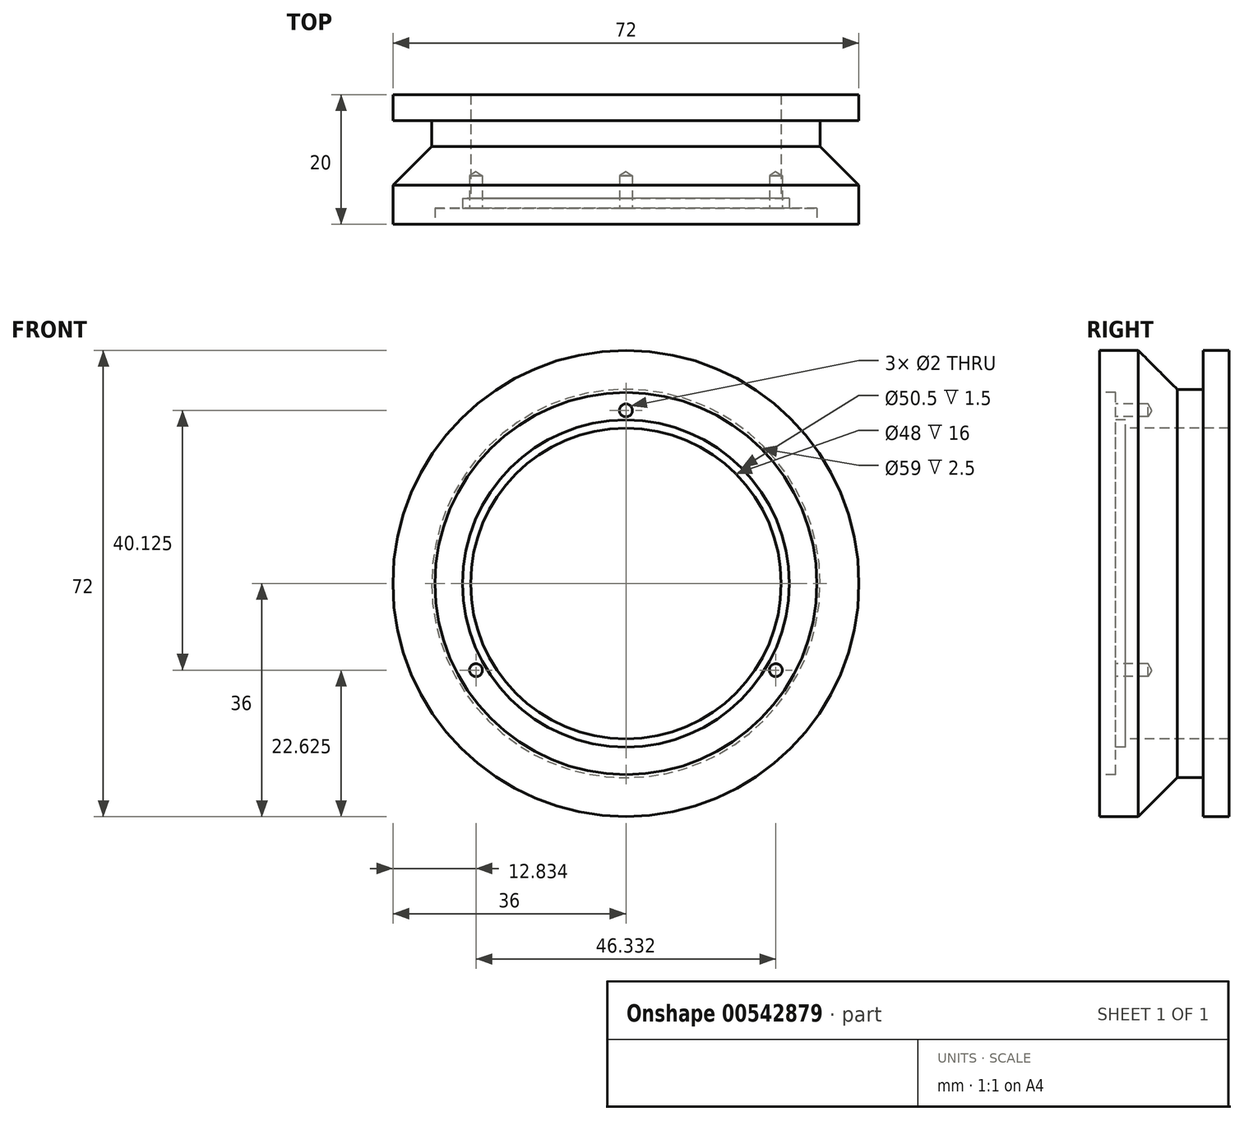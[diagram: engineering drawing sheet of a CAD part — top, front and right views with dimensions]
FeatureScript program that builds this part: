
annotation { "Feature Type Name" : "Feature", "Feature Type Description" : "" }
export const myFeature = defineFeature(function(context is Context, id is Id, definition is map)
    precondition{}
    {
        {
            var Q0;
            Q0=qCreatedBy(makeId("Right.planeOp"),FACE);
            var sketch = newSketch(context, id + "F0", { "sketchPlane" : qUnion([Q0])});
            skLineSegment(sketch, "E0", {"start": v(0, 0) * mm, "end": v(0, 36) * mm});
            skLineSegment(sketch, "E1", {"start": v(0, 36) * mm, "end": v(6, 36) * mm});
            skLineSegment(sketch, "E2", {"start": v(6, 36) * mm, "end": v(12, 30) * mm});
            skLineSegment(sketch, "E3", {"start": v(16, 36) * mm, "end": v(20, 36) * mm});
            skLineSegment(sketch, "E4", {"start": v(20, 36) * mm, "end": v(20, 0) * mm});
            skLineSegment(sketch, "E5", {"start": v(20, 0) * mm, "end": v(0, 0) * mm});
            skLineSegment(sketch, "E6", {"start": v(12, 30) * mm, "end": v(16, 30) * mm});
            skLineSegment(sketch, "E7", {"start": v(16, 30) * mm, "end": v(16, 36) * mm});
            skSolve(sketch);
        }
        {
            var Q0;
            Q0=makeQuery(id+"F0.imprint","IMPRINT",FACE,{"disambiguationData":[TD([[makeQuery(id+"F0.imprint","IMPRINT",EDGE,{"derivedFrom":sQuery(id+"F0.wireOp",EDGE,"E0")}),-1.0]])]});
            var Q1;
            Q1=sQuery(id+"F0.wireOp",EDGE,"E5");
            revolve(context, id + "F1", {"entities" : qUnion([Q0]), "axis" : qUnion([Q1]), "revolveType" : RevolveType.FULL});
        }
        {
            var Q0;
            Q0=makeQuery(id+"F1.opRevolve","SWEPT_FACE",FACE,{"disambiguationData":[OSD([sQuery(id+"F0.wireOp",EDGE,"E0")])]});
            var sketch = newSketch(context, id + "F2", { "sketchPlane" : qUnion([Q0])});
            skCircle(sketch, "E8", {"center": v(0, 0) * mm, "radius": 25.25 * mm});
            skSolve(sketch);
        }
        {
            var Q0;
            Q0=makeQuery(id+"F2.imprint","IMPRINT",FACE,{"disambiguationData":[TD([[makeQuery(id+"F2.imprint","IMPRINT",EDGE,{"derivedFrom":sQuery(id+"F2.wireOp",EDGE,"E8")}),1.0]])]});
            extrude(context, id + "F3", {"entities" : qUnion([Q0]), "operationType" : NewBodyOperationType.REMOVE, "oppositeDirection" : true, "depth" : 4 * mm, "offsetDistance" : 25 * mm});
        }
        {
            var Q0;
            Q0=makeQuery(id+"F3.boolean.opBoolean","COPY",FACE,{"derivedFrom":makeQuery(id+"F3.opExtrude","CAP_FACE",FACE,{"disambiguationData":[OSD([sQuery(id+"F2.wireOp",EDGE,"E8")])],"isStart":false})});
            var sketch = newSketch(context, id + "F4", { "sketchPlane" : qUnion([Q0])});
            skCircle(sketch, "E9", {"center": v(0, 0) * mm, "radius": 24 * mm});
            skSolve(sketch);
        }
        {
            var Q0;
            Q0=makeQuery(id+"F4.imprint","IMPRINT",FACE,{"disambiguationData":[TD([[makeQuery(id+"F4.imprint","IMPRINT",EDGE,{"derivedFrom":sQuery(id+"F4.wireOp",EDGE,"E9")}),1.0]])]});
            extrude(context, id + "F5", {"entities" : qUnion([Q0]), "operationType" : NewBodyOperationType.REMOVE, "endBound" : BoundingType.UP_TO_NEXT, "oppositeDirection" : true, "depth" : 25 * mm, "offsetDistance" : 25 * mm});
        }
        {
            var Q0;
            Q0=makeQuery(id+"F1.opRevolve","SWEPT_FACE",FACE,{"disambiguationData":[OSD([sQuery(id+"F0.wireOp",EDGE,"E0")])]});
            var sketch = newSketch(context, id + "F6", { "sketchPlane" : qUnion([Q0])});
            skCircle(sketch, "E10", {"center": v(0, 0) * mm, "radius": 29.5 * mm});
            skSolve(sketch);
        }
        {
            var Q0;
            Q0=makeQuery(id+"F6.imprint","IMPRINT",FACE,{"disambiguationData":[TD([[makeQuery(id+"F6.imprint","IMPRINT",EDGE,{"derivedFrom":sQuery(id+"F6.wireOp",EDGE,"E10")}),1.0]])]});
            extrude(context, id + "F7", {"entities" : qUnion([Q0]), "operationType" : NewBodyOperationType.REMOVE, "oppositeDirection" : true, "depth" : 2.5 * mm, "offsetDistance" : 25 * mm});
        }
        {
            var Q0;
            Q0=makeQuery(id+"F7.boolean.opBoolean","COPY",FACE,{"derivedFrom":makeQuery(id+"F7.opExtrude","CAP_FACE",FACE,{"disambiguationData":[OSD([sQuery(id+"F2.wireOp",EDGE,"E8"),sQuery(id+"F6.wireOp",EDGE,"E10")])],"isStart":false})});
            var sketch = newSketch(context, id + "F8", { "sketchPlane" : qUnion([Q0])});
            skLineSegment(sketch, "E11", {"start": v(0, 29.5) * mm, "end": v(0, 24) * mm, "construction": true});
            skPoint(sketch, "E12", {"position": v(0, 26.75) * mm});
            skPoint(sketch, "E13.1.0", {"position": v(-23.17, -13.37) * mm});
            skPoint(sketch, "E13.2.0", {"position": v(23.17, -13.37) * mm});
            skPoint(sketch, "E13.center", {"position": v(0, 0) * mm});
            skCircle(sketch, "E14.0", {"center": v(0, 0) * mm, "radius": 24 * mm});
            skSolve(sketch);
        }
        {
            var Q0;
            Q0=sQuery(id+"F8.wireOp",VERTEX,"E12");
            var Q1;
            Q1=sQuery(id+"F8.wireOp",VERTEX,"E13.2.0");
            var Q2;
            Q2=sQuery(id+"F8.wireOp",VERTEX,"E13.1.0");
            var Q3;
            Q3=makeQuery(id+"F1.opRevolve","SWEPT_BODY",BODY,{"disambiguationData":[OSD([sQuery(id+"F0.wireOp",EDGE,"E0"),sQuery(id+"F0.wireOp",EDGE,"E1"),sQuery(id+"F0.wireOp",EDGE,"E2"),sQuery(id+"F0.wireOp",EDGE,"E3"),sQuery(id+"F0.wireOp",EDGE,"E4"),sQuery(id+"F0.wireOp",EDGE,"E5"),sQuery(id+"F0.wireOp",EDGE,"E6"),sQuery(id+"F0.wireOp",EDGE,"E7")])]});
            hole(context, id + "F9", {"style" : HoleStyle.SIMPLE, "endStyle" : HoleEndStyle.BLIND, "holeDiameter" : 2 * mm, "holeDepth" : 5 * mm, "isTappedThrough" : true, "tappedDepth" : 6.5 * mm, "tapClearance" : 3, "locations" : qUnion([Q0, Q1, Q2]), "scope" : qUnion([Q3])});
        }
    });
